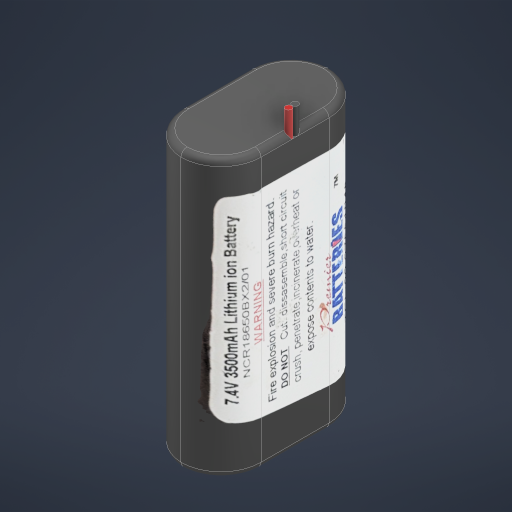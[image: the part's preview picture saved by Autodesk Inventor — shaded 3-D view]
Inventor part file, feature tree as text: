
AUTODESK INVENTOR PART (.ipt)
format: ipt  version: 2023 (Build 270158000, 158)  size: 815,104 bytes
history: native  units: mm
features: other x3, sketch x3, projected_geometry x2, extrude x1, boolean_combine x1, fillet x1, direct_edit x1, move_body x1
ambient origin geometry x8: Origin, YZ Plane, XZ Plane, XY Plane, X Axis, Y Axis, Z Axis, Center Point
bodies: Solid1 (feature_tree), Solid2 (feature_tree), Solid3 (feature_tree), Body1 (feature_tree), Body14 (feature_tree)
feature tree (13):
  extrude  "Extrusion1"  Depth=1.5mm
  boolean_combine  "Combine1"
  other  "Decal1"
  fillet  "Fillet1"  [1 undecoded]
  sketch  "Sketch3"
  direct_edit  "Direct Edit1"
  sketch  "Sketch1"  dims[d0=10.0mm d1=0.0mm d15=1.5mm]
  projected_geometry  "Projected Loop1"
  projected_geometry  "Projected Loop2"
  sketch  "Sketch2"  dims[d16=0.0mm d17=0.0mm d18=-1.5mm]
  other  "Image1"
  other  "Body14:1"
  move_body  "Move1"
note: 1 required parameter value undecoded (feature->parameter linkage not recoverable at this tier; creation-order binding heuristic only, values carry confidence <= 0.55)
